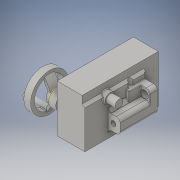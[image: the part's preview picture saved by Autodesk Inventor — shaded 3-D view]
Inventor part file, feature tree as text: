
AUTODESK INVENTOR PART (.ipt)
format: ipt  version: 2016 (Build 200138000, 138)  size: 571,392 bytes
history: native  units: in
note: dims shown in document units (in); Inventor stores cm internally (conversion verified against a paired STEP export)
features: sketch x20, extrude x16, fillet x6, plane x3, loft x2, projected_geometry x2, chamfer x1, other x1
ambient origin geometry x8: Origin, YZ Plane, XZ Plane, XY Plane, X Axis, Y Axis, Z Axis, Center Point
bodies: Solid1 (feature_tree)
feature tree (51):
  extrude  "Extrusion1"  Depth=4.3701in
  extrude  "Extrusion2"  Depth=1.1811in
  extrude  "Extrusion3"  Depth=12.0079in TaperAngle=0.0deg
  extrude  "Extrusion4"  Depth=12.0079in TaperAngle=0.0deg
  extrude  "Extrusion5"  Depth=1.9685in
  extrude  "Extrusion6"  Depth=1.4567in TaperAngle=0.0deg
  extrude  "Extrusion7"  Depth=4.6457in TaperAngle=0.0deg
  fillet  "Fillet2"  Radius=1.7717in
  chamfer  "Chamfer1"  Distance=0.5512in
  fillet  "Fillet3"  Radius=0.7874in
  extrude  "Extrusion8"  Depth=0.5118in TaperAngle=0.0deg
  extrude  "Extrusion9"  Depth=0.315in
  extrude  "Extrusion10"  Depth=0.2559in TaperAngle=0.0deg
  fillet  "Fillet4"  Radius=0.5906in
  extrude  "Extrusion11"  Depth=0.0787in
  extrude  "Extrusion12"  Depth=0.0787in
  sketch  "Sketch14"  dims[d39=0.9449in d40=0.7874in]
  plane  "Work Plane2"
  loft  "Loft1"
  plane  "Work Plane3"
  extrude  "Extrusion13"  Depth=1.1417in
  extrude  "Extrusion15"  Depth=1.7717in
  plane  "Work Plane5"
  sketch  "Sketch22"  dims[d55=3.3071in d56=1.1811in]
  sketch  "Sketch16"  dims[d43=0.2559in d44=0.0in d45=1.7717in]
  loft  "Loft2"
  fillet  "Fillet5"  Radius=0.8268in
  extrude  "Extrusion16"  Depth=1.4173in TaperAngle=0.0deg
  fillet  "Fillet6"  Radius=0.1181in
  fillet  "Fillet7"  Radius=2.7559in
  extrude  "Extrusion17"  Depth=1.1811in
  sketch  "Sketch1"  dims[d0=3.937in d1=4.3701in]
  sketch  "Sketch2"  dims[d2=7.4803in d3=1.1811in]
  sketch  "Sketch3"  dims[d4=5.9843in d5=12.0079in d6=0.0in]
  sketch  "Sketch4"  dims[d7=2.3228in d8=12.0079in d9=0.0in]
  sketch  "Sketch5"  dims[d10=0.7087in d11=1.9685in]
  sketch  "Sketch6"  dims[d12=3.8976in d13=1.4567in d14=0.0in]
  sketch  "Sketch7"  dims[d15=1.5748in d16=4.6457in d17=0.0in d18=1.7717in d19=0.5512in d20=0.0in d21=0.7874in]
  sketch  "Sketch9"  dims[d22=0.7874in d23=0.5118in d24=0.0in]
  sketch  "Sketch10"  dims[d25=2.3622in d26=0.315in]
  sketch  "Sketch11"  dims[d27=0.5906in d28=0.2559in d29=0.0in d31=0.5906in]
  sketch  "Sketch12"  dims[d32=0.5118in d33=0.0787in d34=45.0deg d36=1.1811in]
  sketch  "Sketch13"  dims[d37=1.6142in d38=0.0787in]
  projected_geometry  "Projected Loop1"
  sketch  "Sketch15"  dims[d41=1.0433in d42=1.1417in]
  other  "Edges1"
  sketch  "Sketch18"  dims[d46=1.5748in d47=3.5827in d48=0.8268in d49=0.0in]
  sketch  "Sketch21"  dims[d50=1.2205in d51=1.4173in d52=0.0in d53=0.1181in d54=2.7559in]
  projected_geometry  "Projected Loop4"
  sketch  "Sketch23"  dims[d57=1.1417in d58=0.0in]
  sketch  "Sketch24"  dims[d59=2.2047in d60=0.2756in d61=0.0in d62=0.9449in d63=5.1181in d64=0.0in d65=90.0deg d66=0.0in d67=90.0deg d68=0.6693in d69=2.2047in d71=0.0in d72=90.0deg d75=2.2047in d76=4.7244in d78=0.7874in d79=0.5118in d80=0.2756in d81=0.0in d82=2.7559in d87=5.9843in d88=4.8031in d89=1.063in d90=0.0in d91=1.7717in d92=0.0in d93=90.0deg d94=0.5906in d95=0.7874in d96=2.2047in d97=1.063in d98=0.0in d99=0.0787in d100=0.0787in d101=2.7559in d102=0.0in]
